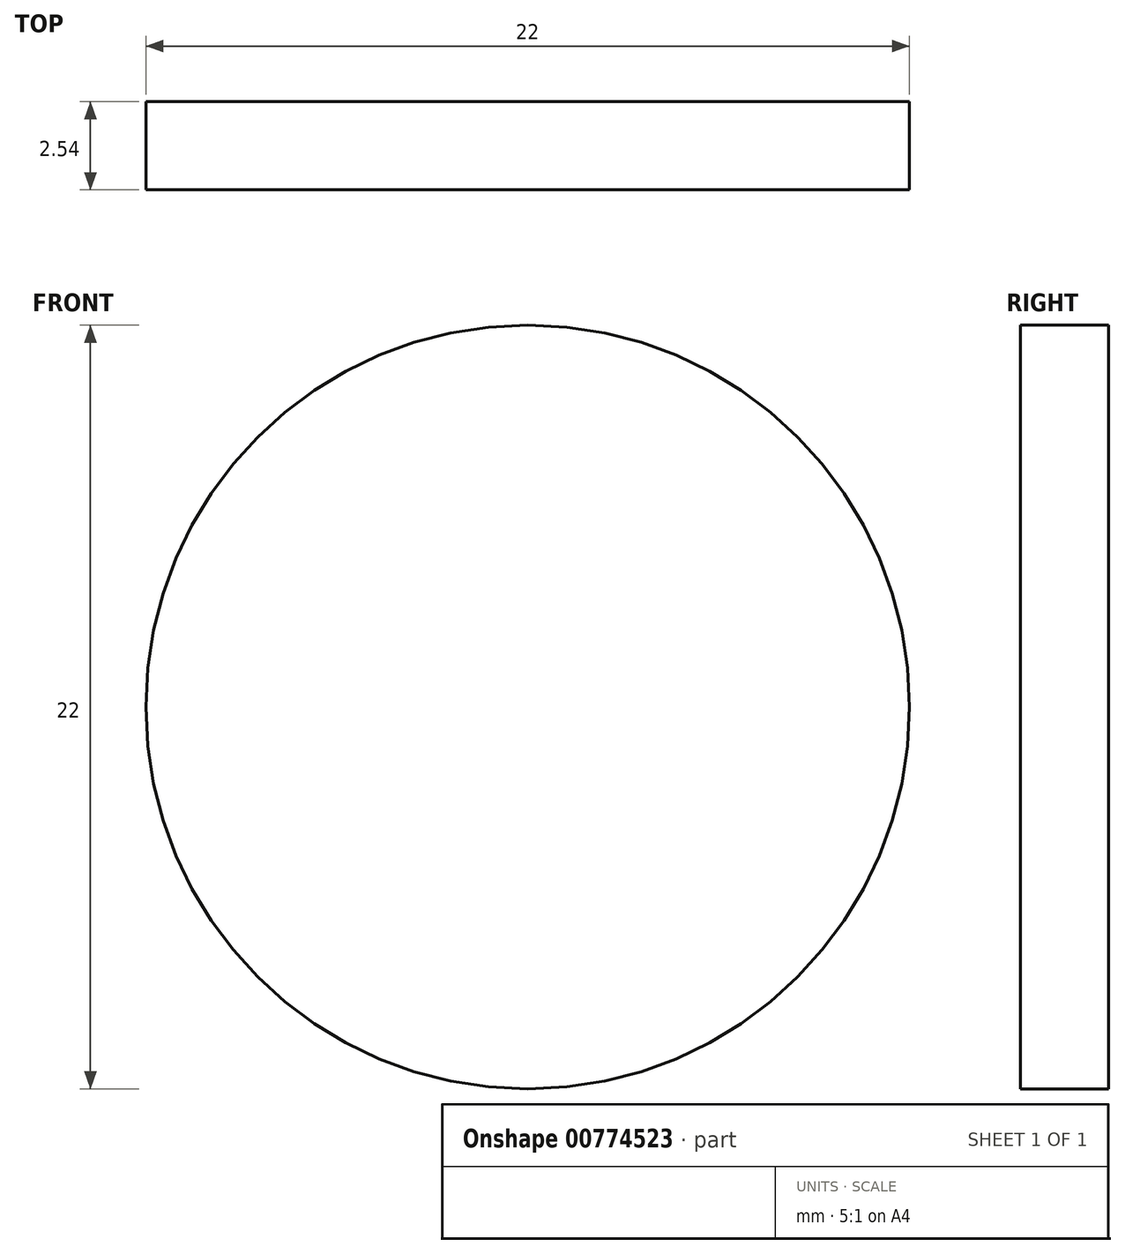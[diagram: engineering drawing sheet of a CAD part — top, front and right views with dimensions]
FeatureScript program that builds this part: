
annotation { "Feature Type Name" : "Feature", "Feature Type Description" : "" }
export const myFeature = defineFeature(function(context is Context, id is Id, definition is map)
    precondition{}
    {
        {
            var Q0;
            Q0=qCreatedBy(makeId("Front.planeOp"),FACE);
            var sketch = newSketch(context, id + "F0", { "sketchPlane" : qUnion([Q0])});
            skCircle(sketch, "E0", {"center": v(0, 0) * mm, "radius": 11 * mm});
            skSolve(sketch);
        }
        {
            var Q0;
            Q0=makeQuery(id+"F0.imprint","IMPRINT",FACE,{"disambiguationData":[TD([[makeQuery(id+"F0.imprint","IMPRINT",EDGE,{"derivedFrom":sQuery(id+"F0.wireOp",EDGE,"E0")}),1.0]])]});
            extrude(context, id + "F1", {"entities" : qUnion([Q0]), "oppositeDirection" : true, "depth" : 2.54 * mm, "offsetDistance" : 25.4 * mm});
        }
    });
